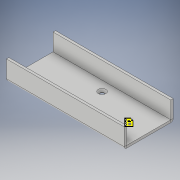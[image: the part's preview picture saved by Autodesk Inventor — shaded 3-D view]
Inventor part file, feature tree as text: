
AUTODESK INVENTOR PART (.ipt)
format: ipt  version: 2017 (Build 210142000, 142)  size: 157,696 bytes
history: native  units: in
note: dims shown in document units (in); Inventor stores cm internally (conversion verified against a paired STEP export)
features: sheet_metal_op x4, sketch x3, other x2, hole x1
ambient origin geometry x8: Origin, YZ Plane, XZ Plane, XY Plane, X Axis, Y Axis, Z Axis, Center Point
bodies: Body1 (feature_tree)
feature tree (10):
  sheet_metal_op  "Face1"
  sheet_metal_op  "Flange1"
  hole  "Hole1"  [1 undecoded]
  sketch  "Sketch2"  dims[d5=6.0in d6=2.25in]
  other  "Plate1"
  sketch  "Sketch3"  dims[d9=0.125in]
  other  "Plate2"
  sheet_metal_op  "Bend1"
  sheet_metal_op  "Corner1"
  sketch  "Sketch4"  dims[d10=0.125in d11=0.0625in d12=0.25in d13=0.125in d14=1.0in d15=90.0deg d16=0.0in d17=0.5in d18=0.125in d19=0.125in d20=1.25in d21=0.625in d22=3.0in d23=0.201in d24=0.38in d25=0.385in d26=0.25in d27=0.5635in d28=0.536in d29=0.8108in]
note: 1 required parameter value undecoded (feature->parameter linkage not recoverable at this tier; creation-order binding heuristic only, values carry confidence <= 0.55)
